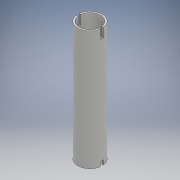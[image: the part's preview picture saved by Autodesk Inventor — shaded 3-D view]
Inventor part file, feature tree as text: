
AUTODESK INVENTOR PART (.ipt)
format: ipt  version: 2018 (Build 220112000, 112)  size: 119,808 bytes
history: native  units: mm
features: extrude x3, sketch x3, other x1
ambient origin geometry x8: Origin, YZ Plane, XZ Plane, XY Plane, X Axis, Y Axis, Z Axis, Center Point
bodies: Body1 (feature_tree)
feature tree (7):
  other  "Sólido1"
  extrude  "Extrusión1"  Depth=23.0mm
  extrude  "Extrusión2"  Depth=3.0mm
  extrude  "Extrusión3"  Depth=3.0mm
  sketch  "Boceto1"  dims[d0=26.35mm d1=23.0mm]
  sketch  "Boceto2"  dims[d2=130.0mm d3=0.0mm d6=3.0mm]
  sketch  "Boceto3"  dims[d7=130.0mm d8=0.0mm d10=3.0mm d11=10.0mm d12=3.0mm d13=30.0mm d14=0.0mm]
